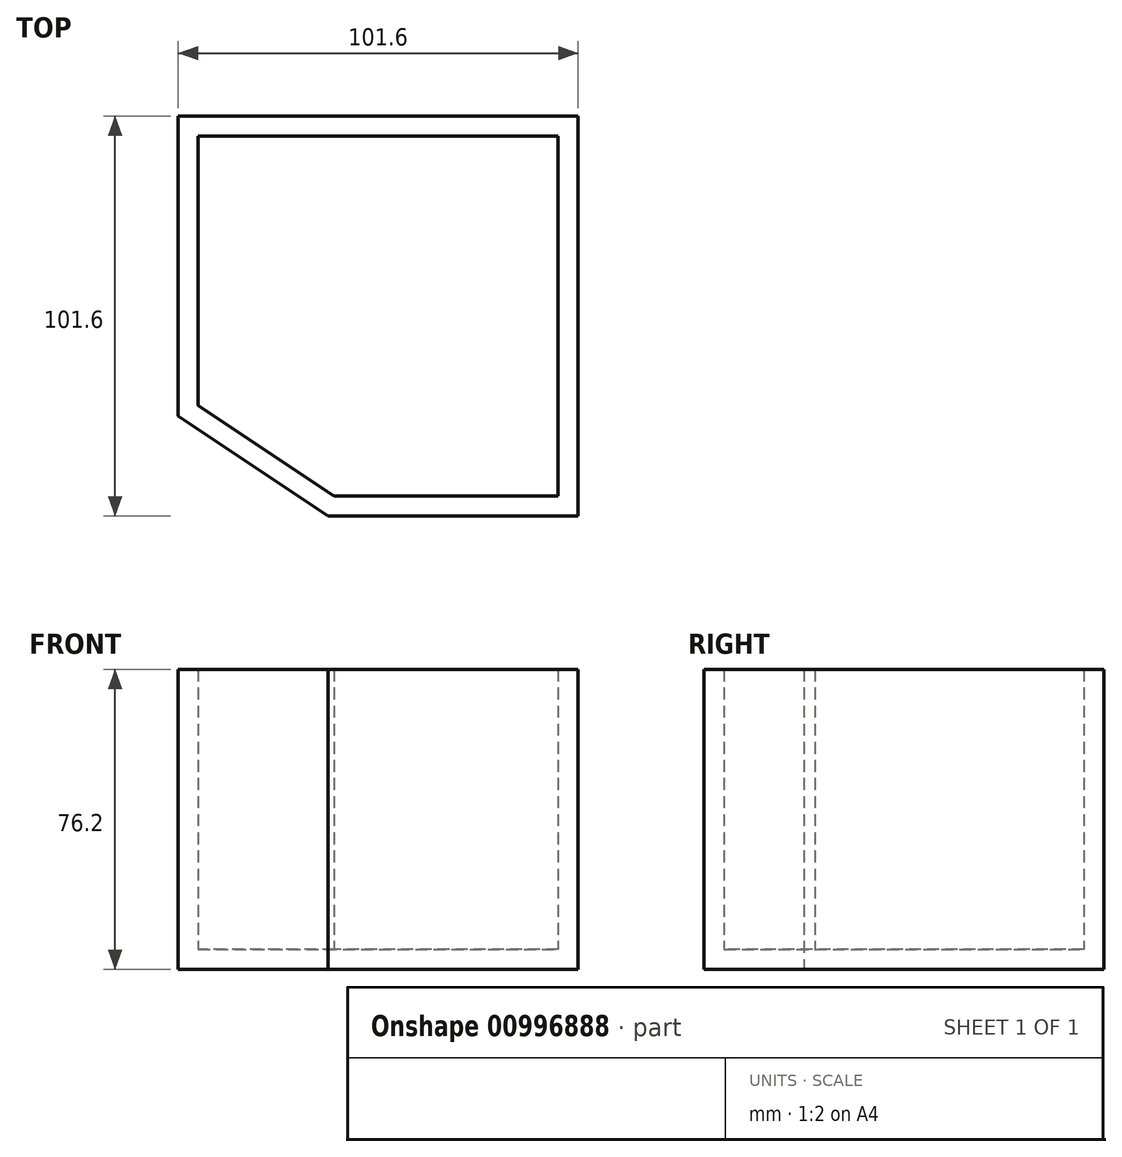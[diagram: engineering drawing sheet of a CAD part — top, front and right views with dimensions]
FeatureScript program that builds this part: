
annotation { "Feature Type Name" : "Feature", "Feature Type Description" : "" }
export const myFeature = defineFeature(function(context is Context, id is Id, definition is map)
    precondition{}
    {
        {
            var Q0;
            Q0=qCreatedBy(makeId("Top.planeOp"),FACE);
            var sketch = newSketch(context, id + "F0", { "sketchPlane" : qUnion([Q0])});
            skLineSegment(sketch, "E0", {"start": v(-50.66, -34.43) * mm, "end": v(-50.66, 41.77) * mm});
            skLineSegment(sketch, "E1", {"start": v(-50.66, 41.77) * mm, "end": v(50.94, 41.77) * mm});
            skLineSegment(sketch, "E2", {"start": v(50.94, 41.77) * mm, "end": v(50.94, -59.83) * mm});
            skLineSegment(sketch, "E3", {"start": v(50.94, -59.83) * mm, "end": v(-12.56, -59.83) * mm});
            skLineSegment(sketch, "E4", {"start": v(-12.56, -59.83) * mm, "end": v(-50.66, -34.43) * mm});
            skSolve(sketch);
        }
        {
            var Q0;
            Q0 = qSketchRegion(id + "F0", true);
            extrude(context, id + "F1", {"entities" : qUnion([Q0]), "depth" : 76.2 * mm, "offsetDistance" : 25.4 * mm});
        }
        {
            var Q0;
            Q0=makeQuery(id+"F1.opExtrude","CAP_FACE",FACE,{"disambiguationData":[OSD([sQuery(id+"F0.wireOp",EDGE,"E0"),sQuery(id+"F0.wireOp",EDGE,"E1"),sQuery(id+"F0.wireOp",EDGE,"E2"),sQuery(id+"F0.wireOp",EDGE,"E3"),sQuery(id+"F0.wireOp",EDGE,"E4")])],"isStart":false});
            shell(context, id + "F2", {"entities" : qUnion([Q0]), "thickness" : 5.08 * mm});
        }
    });
